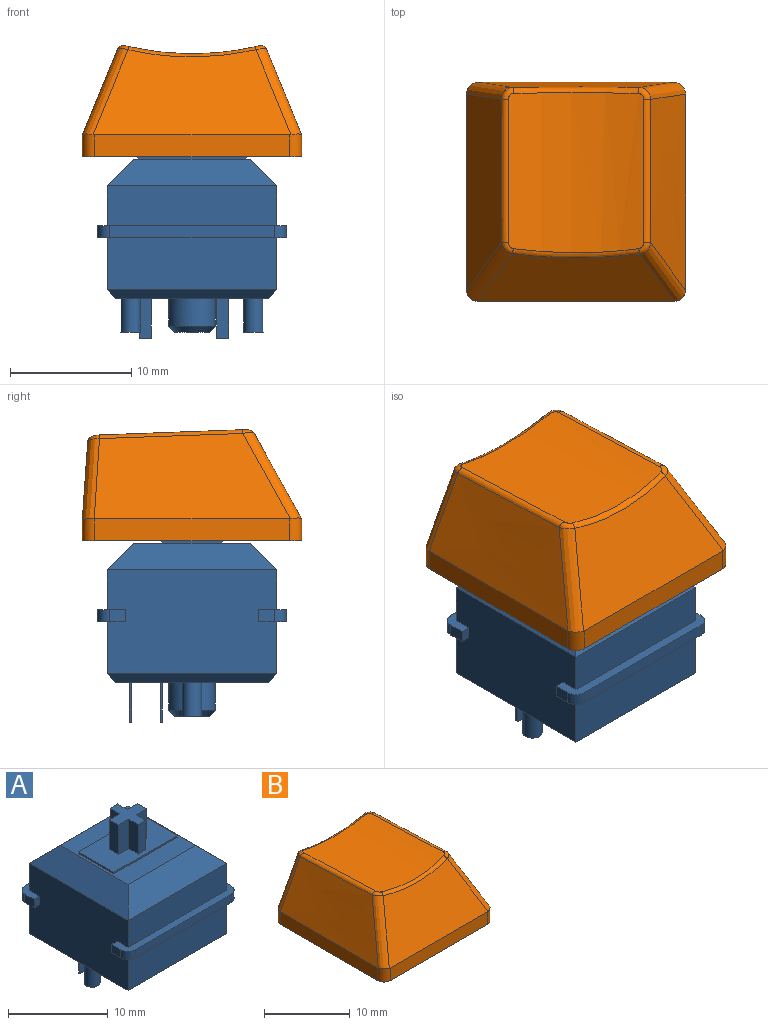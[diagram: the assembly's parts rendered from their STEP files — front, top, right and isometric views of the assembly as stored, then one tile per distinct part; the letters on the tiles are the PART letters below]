
ASSEMBLY  parts=2 mates=1
PART A: 69 faces, bbox 15.6x15.6x18.6 mm
  f0: plane 15.6x2.3mm, normal (0,0,-1), area 14.4mm2, adj f2,f3,f28,f30,f35,f60,f62,f63
  f1: plane 15.6x2.3mm, normal (0,0,-1), area 14.4mm2, adj f28,f30,f33,f34,f36,f59,f61,f64
  f2: plane 1.3x1mm, normal (1,0,0), area 1.3mm2, adj f0,f32,f62,f66
  f3: plane 1.3x1mm, normal (-1,0,0), area 1.3mm2, adj f0,f32,f63,f68
  f4: plane 15.6x2.3mm, normal (0,0,1), area 14.4mm2, adj f28,f30,f31,f33,f34,f36,f61,f64
  f5: plane 14x2.2mm, normal (-0.71,0,0.71), area 36.7mm2, adj f6,f7,f26,f30
  f6: plane 14x2.2mm, normal (0,-0.71,0.71), area 36.7mm2, adj f5,f7,f27,f31
  f7: plane 9.6x9.6mm, normal (0,0,1), area 47.2mm2, adj f5,f6,f8,f9,f10,f11,f26,f27
  f8: plane 5x0.2mm, normal (1,0,0), area 1mm2, adj f7,f9,f11,f12
  f9: plane 9x0.2mm, normal (0,1,0), area 1.8mm2, adj f7,f8,f10,f12
  f10: plane 5x0.2mm, normal (-1,0,0), area 1mm2, adj f7,f9,f11,f12
  f11: plane 9x0.2mm, normal (0,-1,0), area 1.8mm2, adj f7,f8,f10,f12
  f12: plane 9x5mm, normal (0,0,1), area 36.9mm2, adj f8,f9,f10,f11,f13,f14,f15,f16
  f13: plane 3.6x1.35mm, normal (1,0,0), area 4.9mm2, adj f12,f14,f24,f25
  f14: plane 3.6x1.08mm, normal (0,1,0), area 3.9mm2, adj f12,f13,f15,f25
  f15: plane 3.6x1.35mm, normal (-1,0,0), area 4.9mm2, adj f12,f14,f16,f25
  f16: plane 3.6x1.46mm, normal (0,1,0), area 5.3mm2, adj f12,f15,f17,f25
  f17: plane 3.6x1.3mm, normal (-1,0,0), area 4.7mm2, adj f12,f16,f18,f25
  f18: plane 3.6x1.46mm, normal (0,-1,0), area 5.3mm2, adj f12,f17,f19,f25
  f19: plane 3.6x1.35mm, normal (-1,0,0), area 4.9mm2, adj f12,f18,f20,f25
  f20: plane 3.6x1.08mm, normal (0,-1,0), area 3.9mm2, adj f12,f19,f21,f25
  f21: plane 3.6x1.35mm, normal (1,0,0), area 4.9mm2, adj f12,f20,f22,f25
  f22: plane 3.6x1.46mm, normal (0,-1,0), area 5.3mm2, adj f12,f21,f23,f25
  f23: plane 3.6x1.3mm, normal (1,0,0), area 4.7mm2, adj f12,f22,f24,f25
  f24: plane 3.6x1.46mm, normal (0,1,0), area 5.3mm2, adj f12,f13,f23,f25
  f25: plane 4x4mm, normal (0,0,1), area 8.1mm2, adj f13,f14,f15,f16,f17,f18,f19,f20
  f26: plane 14x2.2mm, normal (0,0.71,0.71), area 36.7mm2, adj f5,f7,f27,f29
  f27: plane 14x2.2mm, normal (0.71,0,0.71), area 36.7mm2, adj f6,f7,f26,f28
  f28: plane 14x8.6mm, normal (1,0,0), area 117.4mm2, adj f0,f1,f4,f27,f29,f31,f32,f55
  f29: plane 14x3.3mm, normal (0,1,0), area 46.2mm2, adj f26,f28,f30,f32
  f30: plane 14x8.6mm, normal (-1,0,0), area 117.4mm2, adj f0,f1,f4,f5,f29,f31,f32,f57
  f31: plane 14x3.3mm, normal (0,-1,0), area 46.2mm2, adj f4,f6,f28,f30
  f32: plane 15.6x2.3mm, normal (0,0,1), area 14.4mm2, adj f2,f3,f28,f29,f30,f35,f62,f63
  f33: plane 13.6x1mm, normal (0,-1,0), area 13.6mm2, adj f1,f4,f61,f64
  f34: plane 1.3x1mm, normal (1,0,0), area 1.3mm2, adj f1,f4,f61,f65
  f35: plane 13.6x1mm, normal (0,1,0), area 13.6mm2, adj f0,f32,f62,f63
  f36: plane 1.3x1mm, normal (-1,0,0), area 1.3mm2, adj f1,f4,f64,f67
  f37: plane 2.85x2.85mm, normal (0,0,-1), area 6.4mm2, adj f38
  f38: cone r=1.43mm half-angle=45deg, axis (0,0,1), area 7.4mm2, adj f37,f43
  f39: plane 1x0.2mm, normal (0,0,-1), area 0.2mm2, adj f44,f45,f46,f47
  f40: plane 1x0.2mm, normal (0,0,-1), area 0.2mm2, adj f48,f49,f50,f51
  f41: plane 1.6x1.6mm, normal (0,0,-1), area 2mm2, adj f52
  f42: plane 1.6x1.6mm, normal (0,0,-1), area 2mm2, adj f53
  f43: cylinder r=1.93mm len=3.85mm, axis (0,0,1), area 27.8mm2, adj f38,f54
  f44: plane 3.3x0.2mm, normal (-1,0,0), area 0.7mm2, adj f39,f45,f47,f54
  f45: plane 3.3x1mm, normal (0,1,0), area 3.3mm2, adj f39,f44,f46,f54
  f46: plane 3.3x0.2mm, normal (1,0,0), area 0.7mm2, adj f39,f45,f47,f54
  f47: plane 3.3x1mm, normal (0,-1,0), area 3.3mm2, adj f39,f44,f46,f54
  f48: plane 3.3x0.2mm, normal (-1,0,0), area 0.7mm2, adj f40,f49,f51,f54
  f49: plane 3.3x1mm, normal (0,1,0), area 3.3mm2, adj f40,f48,f50,f54
  f50: plane 3.3x0.2mm, normal (1,0,0), area 0.7mm2, adj f40,f49,f51,f54
  f51: plane 3.3x1mm, normal (0,-1,0), area 3.3mm2, adj f40,f48,f50,f54
  f52: cylinder r=0.8mm len=2.8mm, axis (0,0,1), area 14.1mm2, adj f41,f54
  f53: cylinder r=0.8mm len=2.8mm, axis (0,0,1), area 14.1mm2, adj f42,f54
  f54: plane 12.6x12.6mm, normal (0,0,-1), area 142.7mm2, adj f43,f44,f45,f46,f47,f48,f49,f50
  f55: plane 14x0.7mm, normal (0.71,0,-0.71), area 13.2mm2, adj f28,f54,f56,f58
  f56: plane 14x0.7mm, normal (0,0.71,-0.71), area 13.2mm2, adj f54,f55,f57,f60
  f57: plane 14x0.7mm, normal (-0.71,0,-0.71), area 13.2mm2, adj f30,f54,f56,f58
  f58: plane 14x0.7mm, normal (0,-0.71,-0.71), area 13.2mm2, adj f54,f55,f57,f59
  f59: plane 14x4.3mm, normal (0,-1,0), area 60.2mm2, adj f1,f28,f30,f58
  f60: plane 14x4.3mm, normal (0,1,0), area 60.2mm2, adj f0,f28,f30,f56
  f61: cylinder r=1mm len=1mm, axis (0,0,-1), area 1.6mm2, adj f1,f4,f33,f34
  f62: cylinder r=1mm len=1mm, axis (0,0,1), area 1.6mm2, adj f0,f2,f32,f35
  f63: cylinder r=1mm len=1mm, axis (0,0,-1), area 1.6mm2, adj f0,f3,f32,f35
  f64: cylinder r=1mm len=1mm, axis (0,0,1), area 1.6mm2, adj f1,f4,f33,f36
  f65: plane 1x0.8mm, normal (0,1,0), area 0.8mm2, adj f1,f4,f28,f34
  f66: plane 1x0.8mm, normal (0,-1,0), area 0.8mm2, adj f0,f2,f28,f32
  f67: plane 1x0.8mm, normal (0,1,0), area 0.8mm2, adj f1,f4,f30,f36
  f68: plane 1x0.8mm, normal (0,-1,0), area 0.8mm2, adj f0,f3,f30,f32
PART B: 50 faces, bbox 21.6x22.4x13.2 mm
  f0: plane 18.1x18.1mm, normal (0,0,-1), area 67.5mm2, adj f1,f2,f3,f4,f10,f12,f14,f16
  f1: plane 16.1x1.8mm, normal (1,0,0), area 29mm2, adj f0,f8,f10,f16
  f2: plane 16.11x1.81mm, normal (0,1,0), area 29mm2, adj f0,f5,f14,f15,f16,f17
  f3: plane 16.1x1.8mm, normal (-1,0,0), area 29mm2, adj f0,f6,f12,f14
  f4: plane 16.1x1.8mm, normal (0,-1,0), area 29mm2, adj f0,f7,f10,f12
  f5: plane 15.98x6.33mm, normal (0,1,0.07), area 79.8mm2, adj f2,f15,f17,f20
  f6: bspline ~18.1x7.49mm, area 104.4mm2, adj f3,f12,f13,f14,f15,f19
  f7: plane 16.33x7.03mm, normal (0,-0.87,0.48), area 103.3mm2, adj f4,f10,f11,f12,f13,f23
  f8: bspline ~18.1x7.49mm, area 104.4mm2, adj f1,f10,f11,f16,f17,f24
  f9: cylinder r=22.9mm len=12.87mm, axis (0,1,-0.04), area 144.5mm2, adj f18,f19,f20,f21,f22,f23,f24,f25
  f10: cylinder r=1mm len=1.88mm, axis (0,0,-1), area 2.9mm2, adj f0,f1,f4,f7,f8,f11
  f11: bspline ~9.11x5.74mm, area 11.9mm2, adj f7,f8,f10,f25
  f12: cylinder r=1mm len=1.88mm, axis (0,0,1), area 2.9mm2, adj f0,f3,f4,f6,f7,f13
  f13: bspline ~9.11x5.74mm, area 11.9mm2, adj f6,f7,f12,f21
  f14: cylinder r=1mm len=1.81mm, axis (0,0,-1), area 2.8mm2, adj f0,f2,f3,f6,f15
  f15: bspline ~11.15x5.6mm, area 11mm2, adj f2,f5,f6,f14,f18
  f16: cylinder r=1mm len=1.81mm, axis (0,0,1), area 2.8mm2, adj f0,f1,f2,f8,f17
  f17: bspline ~11.16x5.6mm, area 11mm2, adj f2,f5,f8,f16,f22
  f18: bspline ~1.21x1.09mm, area 0.9mm2, adj f9,f15,f19,f20
  f19: bspline ~17.91x1.05mm, area 8.4mm2, adj f6,f9,f18,f21
  f20: bspline ~10.48x1.05mm, area 7.6mm2, adj f5,f9,f18,f22
  f21: bspline ~1.23x1.13mm, area 0.7mm2, adj f9,f13,f19,f23
  f22: bspline ~1.25x1.04mm, area 0.9mm2, adj f9,f17,f20,f24
  f23: bspline ~10.58x0.84mm, area 5.8mm2, adj f7,f9,f21,f25
  f24: bspline ~17.91x1.05mm, area 8.4mm2, adj f8,f9,f22,f25
  f25: bspline ~1.23x1.02mm, area 0.7mm2, adj f9,f11,f23,f24
  f26: plane 16.11x1.61mm, normal (-1,0,0), area 25.7mm2, adj f0,f27,f29,f32,f33
  f27: plane 16.1x1.77mm, normal (0,-1,0), area 28.4mm2, adj f0,f26,f28,f30,f31,f33
  f28: plane 16.11x1.61mm, normal (1,0,0), area 25.7mm2, adj f0,f27,f29,f31,f32
  f29: plane 16.1x1.54mm, normal (0,1,0), area 24.8mm2, adj f0,f26,f28,f32
  f30: plane 16.08x6.01mm, normal (0,-1,-0.07), area 74.4mm2, adj f27,f31,f33,f34
  f31: offset ~20.1x9.49mm, area 95.9mm2, adj f27,f28,f30,f32,f34
  f32: plane 16.73x7.17mm, normal (0,0.87,-0.48), area 95.8mm2, adj f26,f28,f29,f31,f33,f34
  f33: offset ~20.1x9.49mm, area 95.9mm2, adj f26,f27,f30,f32,f34
  f34: cylinder r=23.9mm len=12.1mm, axis (0,1,-0.04), area 108.1mm2, adj f30,f31,f32,f33,f46
  f35: plane 7.29x1.35mm, normal (-1,0,0), area 9.8mm2, adj f36,f44,f45,f49
  f36: plane 7.37x1.5mm, normal (0,-1,0), area 11mm2, adj f35,f37,f45,f49
  f37: plane 7.41x1.3mm, normal (-1,0,0), area 9.6mm2, adj f36,f38,f45,f49
  f38: plane 7.41x1.5mm, normal (0,1,0), area 11mm2, adj f37,f39,f45,f49
  f39: plane 7.38x1.35mm, normal (-1,0,0), area 9.9mm2, adj f38,f40,f45,f49
  f40: plane 7.38x1mm, normal (0,1,0), area 7.4mm2, adj f39,f41,f45,f49
  f41: plane 7.38x1.35mm, normal (1,0,0), area 9.9mm2, adj f40,f42,f45,f49
  f42: plane 7.41x1.5mm, normal (0,1,0), area 11mm2, adj f41,f43,f45,f49
  f43: plane 7.41x1.3mm, normal (1,0,0), area 9.6mm2, adj f42,f45,f47,f49
  f44: plane 7.24x1mm, normal (0,-1,0), area 7.2mm2, adj f35,f45,f48,f49
  f45: plane 5.5x5.5mm, normal (0,0,-1), area 15.9mm2, adj f35,f36,f37,f38,f39,f40,f41,f42
  f46: cylinder r=2.75mm len=7.46mm, axis (0,0,-1), area 129mm2, adj f34,f45
  f47: plane 7.37x1.5mm, normal (0,-1,0), area 11mm2, adj f43,f45,f48,f49
  f48: plane 7.29x1.35mm, normal (1,0,0), area 9.8mm2, adj f44,f45,f47,f49
  f49: cylinder r=23.9mm len=4mm, axis (0,1,-0.04), area 7.9mm2, adj f35,f36,f37,f38,f39,f40,f41,f42
PLACE A at identity fixed
PLACE B t=(0,0,11.7)mm
MATE fastened A.f38 <-> B.f46  axis (0,0,1) through (0,0,11.7)mm
